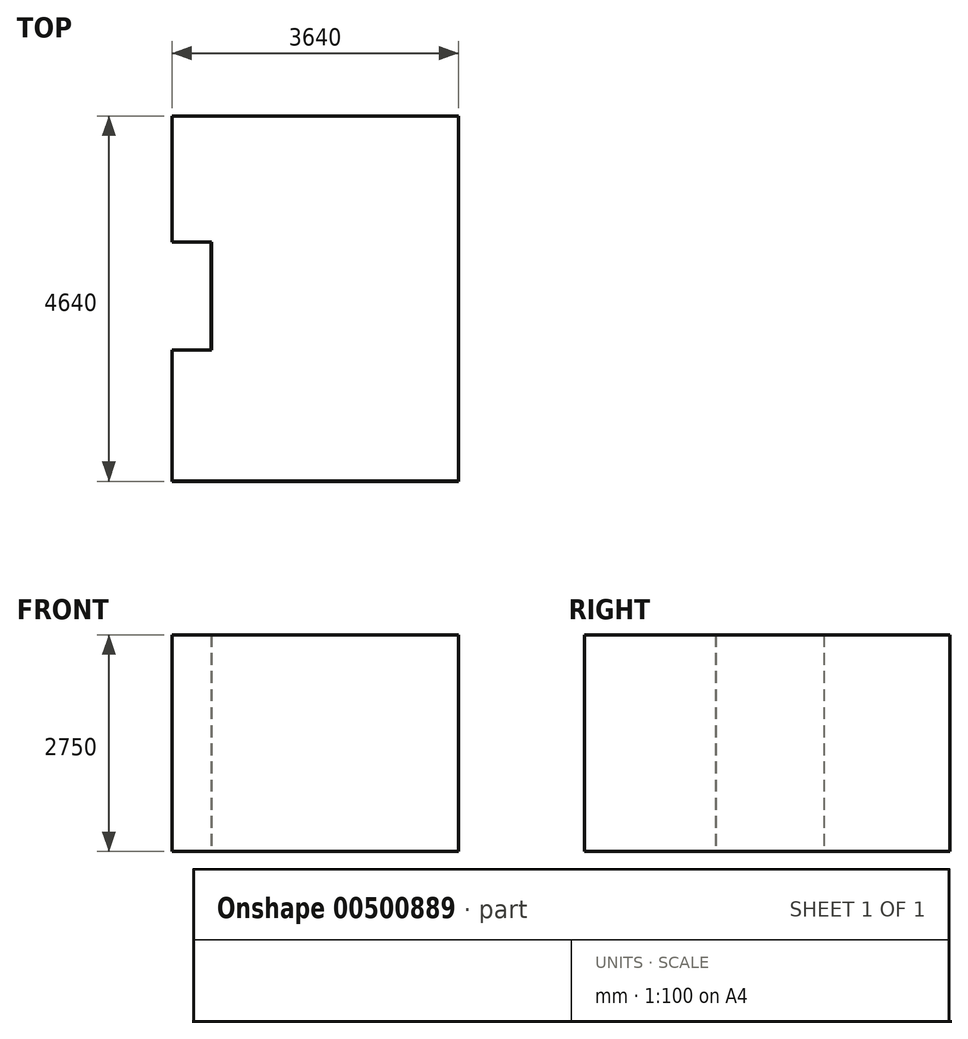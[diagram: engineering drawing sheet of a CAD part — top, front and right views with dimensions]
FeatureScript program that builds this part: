
annotation { "Feature Type Name" : "Feature", "Feature Type Description" : "" }
export const myFeature = defineFeature(function(context is Context, id is Id, definition is map)
    precondition{}
    {
        {
            var Q0;
            Q0=qCreatedBy(makeId("Top.planeOp"),FACE);
            var sketch = newSketch(context, id + "F0", { "sketchPlane" : qUnion([Q0])});
            skLineSegment(sketch, "E0.bottom", {"start": v(0, 0) * mm, "end": v(3640, 0) * mm});
            skLineSegment(sketch, "E0.top", {"start": v(0, 4640) * mm, "end": v(3640, 4640) * mm});
            skLineSegment(sketch, "E0.left", {"start": v(0, 0) * mm, "end": v(0, 1670) * mm});
            skLineSegment(sketch, "E0.right", {"start": v(3640, 0) * mm, "end": v(3640, 4640) * mm});
            skLineSegment(sketch, "E1.bottom", {"start": v(0, 1670) * mm, "end": v(500, 1670) * mm});
            skLineSegment(sketch, "E1.top", {"start": v(0, 3040) * mm, "end": v(500, 3040) * mm});
            skLineSegment(sketch, "E1.right", {"start": v(500, 1670) * mm, "end": v(500, 3040) * mm});
            skLineSegment(sketch, "E2.trimOffspring", {"start": v(0, 3040) * mm, "end": v(0, 4640) * mm});
            skSolve(sketch);
        }
        {
            var Q0;
            Q0 = qSketchRegion(id + "F0", true);
            extrude(context, id + "F1", {"entities" : qUnion([Q0]), "depth" : 2750 * mm, "offsetDistance" : 25 * mm});
        }
        {
            var Q0;
            Q0=makeQuery(id+"F1.opExtrude","CAP_FACE",FACE,{"disambiguationData":[OSD([sQuery(id+"F0.wireOp",EDGE,"E0.bottom"),sQuery(id+"F0.wireOp",EDGE,"E0.top"),sQuery(id+"F0.wireOp",EDGE,"E0.left"),sQuery(id+"F0.wireOp",EDGE,"E0.right"),sQuery(id+"F0.wireOp",EDGE,"E1.bottom"),sQuery(id+"F0.wireOp",EDGE,"E1.top"),sQuery(id+"F0.wireOp",EDGE,"E1.right"),sQuery(id+"F0.wireOp",EDGE,"E2.trimOffspring")])],"isStart":false});
            shell(context, id + "F2", {"entities" : qUnion([Q0]), "thickness" : 2.5 * mm});
        }
    });
